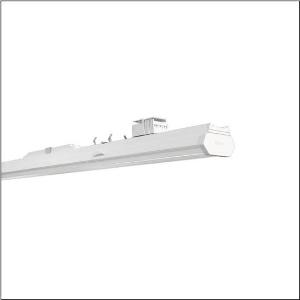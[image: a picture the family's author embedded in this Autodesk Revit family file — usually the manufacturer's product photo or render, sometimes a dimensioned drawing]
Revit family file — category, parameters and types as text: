
# Revit family: licross_21_protected_ho_52tp11dn4e5s
name_source: partatom
category: Lighting Fixtures
units: mm (PartAtom-declared; Revit-internal decimal feet)

## family parameters
Cut with Voids When Loaded = No
Host = Face
Light Source = No
Part Type = Normal
Room Calculation Point = No
Round Connector Dimension = Use Diameter
Shared = No

## types (1)
- --- (1 x LED, 14920 lm, 84.9 W, 4000K)
    Apparent Load = 85 VA
    CIE Flux Codes = 84 94 98 99 100
    Color Rendering = 80
    Color Temperature = 4000K
    Default Elevation = 1800 mm
    Description = Licross 21 Protected HO, luminaire insert, of sheet steel, galvanised, coil coated, white, length: 1.500mm, width: 90mm, height: 103mm, LED rated luminous flux: 14.920lm, light colour: 840, SDCM (Standard Deviation of Colour Matching)MacAdam ≤ 3 SDCM (initial), control gear: DALI 2, with plug, 5-pole, with phase selection, mains connection: 220..240V, AC, 50/60Hz, rated input power: 85W, internal wiring halogen-free, primary light control with lens, of plastic, primary optical cover: cover, of PMMA, light emission: direct distribution, primary light characteristic: symmetric, protection rating (complete): IP64, insulation class (complete): insulation class I (protective earthing), certification: CE, ENEC, VDE, UKCA, protection symbol: D if used in an environment with conductive dust loads with corresponding accessories, impact resistance: IK06, permissible ambient temperature for indoor applications: -25..+35°C, corresponds to IFS (International Featured Standards) requirements for safety and quality in the food industry, reducing of maximum allowable ambient temperature of 5°C with ceiling mounting, LABS conformity tested according to VDMA 24364:2018-05, The light source and the operating device comply with the requirements of the Ecodesign Regulation (EU) 2019/2020 and are replaceable in accordance with this regulation, packaging unit: 1 piece
    Height = 92 mm
    Lamp = 1 x LED
    Lamp Light Flux = 14920 lm
    Lamp Power = 84.9 W
    Lamp count = 1
    Length = 1500 mm
    Luminous efficacy = 176 lm/W
    Manufacturer = Siteco
    ModVariant = No
    Model = 52TP11DN4E5S
    Mounting Place = Ceiling
    Mounting Type = Pendant
    Number of Poles = 1
    OnlyDefault = Yes
    Power Factor = 1
    Product Name = Licross 21 Protected HO
    Product group = luminaire insert | ceiling pendant
    ProductGroupID = 901
    Protection Class = Protection class I
    Protection Degree = IP 64
    RLX_Detail_Level = 1
    RLX_Emergency_Light_Flux = 0 lm
    RLX_Emergency_Type = 0
    RLX_Emergency_Type_DB = No
    RlxData = <blob elided: 24593 chars, md5=99d4ec67>
    Socket = socket
    Standby Power = 0 W
    System Light Flux = 14920 lm
    System Power = 85 W
    Type Comments = factory setting: luminous flux: 100 % | dim-lin: 254 | 484 mA
    Type Image = l_1256148.jpg
    URL = http://relux.com
    VarID = @adj_130147
    Voltage = 0 V
    Weight = 0.00 kg
    Width = 88 mm

## geometry (parser evidence)
native form markers: Blend x4, Sweep x11
no freeform markers — native parametric forms only
